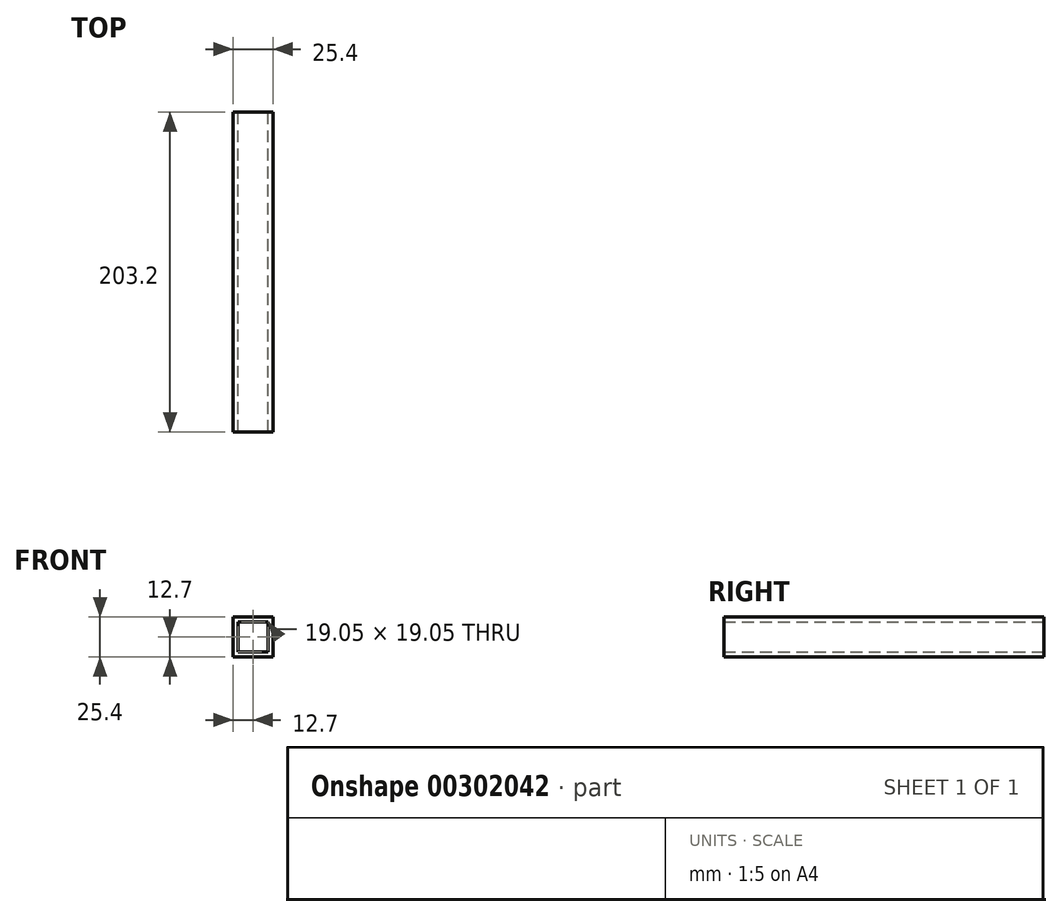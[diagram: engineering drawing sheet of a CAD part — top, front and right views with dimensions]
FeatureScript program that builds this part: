
annotation { "Feature Type Name" : "Feature", "Feature Type Description" : "" }
export const myFeature = defineFeature(function(context is Context, id is Id, definition is map)
    precondition{}
    {
        {
            var Q0;
            Q0=qCreatedBy(makeId("Front.planeOp"),FACE);
            var sketch = newSketch(context, id + "F0", { "sketchPlane" : qUnion([Q0])});
            skLineSegment(sketch, "E0.bottom", {"start": v(-12.7, 12.7) * mm, "end": v(12.7, 12.7) * mm});
            skLineSegment(sketch, "E0.top", {"start": v(-12.7, -12.7) * mm, "end": v(12.7, -12.7) * mm});
            skLineSegment(sketch, "E0.left", {"start": v(-12.7, 12.7) * mm, "end": v(-12.7, -12.7) * mm});
            skLineSegment(sketch, "E0.right", {"start": v(12.7, 12.7) * mm, "end": v(12.7, -12.7) * mm});
            skPoint(sketch, "E0.middle", {"position": v(0, 0) * mm});
            skLineSegment(sketch, "E1.bottom", {"start": v(-9.53, 9.52) * mm, "end": v(9.53, 9.52) * mm});
            skLineSegment(sketch, "E1.top", {"start": v(-9.53, -9.52) * mm, "end": v(9.53, -9.52) * mm});
            skLineSegment(sketch, "E1.left", {"start": v(-9.53, 9.53) * mm, "end": v(-9.53, -9.53) * mm});
            skLineSegment(sketch, "E1.right", {"start": v(9.53, 9.53) * mm, "end": v(9.53, -9.53) * mm});
            skSolve(sketch);
        }
        {
            var Q0;
            Q0 = qSketchRegion(id + "F0", true);
            extrude(context, id + "F1", {"entities" : qUnion([Q0]), "depth" : 203.2 * mm});
        }
    });
